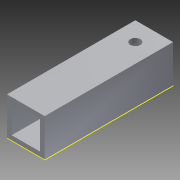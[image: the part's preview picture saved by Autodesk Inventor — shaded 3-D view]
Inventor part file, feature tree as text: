
AUTODESK INVENTOR PART (.ipt)
format: ipt  version: 2014 SP1 (Build 180222100, 222)  size: 107,008 bytes
history: native  units: in
note: dims shown in document units (in); Inventor stores cm internally (conversion verified against a paired STEP export)
features: reference x4, extrude x3, sketch x3
ambient origin geometry x8: Origin, YZ Plane, XZ Plane, XY Plane, X Axis, Y Axis, Z Axis, Center Point
bodies: Solid1 (feature_tree)
feature tree (10):
  extrude  "Extrusion1"  Depth=1.0in
  extrude  "Extrusion2"  Depth=3.4in TaperAngle=0.0deg
  extrude  "Extrusion3"  Depth=1.0in
  sketch  "Sketch1"  dims[d0=1.0in d1=1.0in]
  sketch  "Sketch2"  dims[d2=0.125in d3=3.4in d4=0.0in]
  sketch  "Sketch3"  dims[d5=0.5in d6=0.266in d7=3.4in d8=0.0in d9=1.0in d10=0.0in]
  reference  "Reference1"
  reference  "Reference2"
  reference  "Reference3"
  reference  "Reference4"
